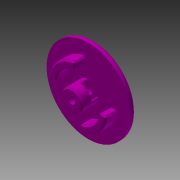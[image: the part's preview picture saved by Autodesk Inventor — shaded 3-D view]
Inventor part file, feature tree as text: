
AUTODESK INVENTOR PART (.ipt)
format: ipt  version: 2014 (Build 180170000, 170)  size: 237,056 bytes
history: native  units: in
note: dims shown in document units (in); Inventor stores cm internally (conversion verified against a paired STEP export)
features: extrude x8, sketch x8, fillet x4, pattern_circular x1, plane x1, chamfer x1
ambient origin geometry x8: Origin, YZ Plane, XZ Plane, XY Plane, X Axis, Y Axis, Z Axis, Center Point
bodies: Solid1 (feature_tree)
feature tree (23):
  extrude  "Extrusion1"  Depth=0.1in TaperAngle=0.0deg
  extrude  "Extrusion2"  Depth=0.3in TaperAngle=0.0deg
  extrude  "Extrusion3"  Depth=0.335in TaperAngle=0.0deg
  extrude  "Extrusion4"  Depth=0.0478in
  pattern_circular  "Circular Pattern1"  Count=2 Angle=360.0deg
  extrude  "Extrusion5"  Depth=0.02in
  extrude  "Extrusion6"  Depth=0.26in TaperAngle=0.0deg
  plane  "Work Plane1"
  extrude  "Extrusion7"  Depth=0.02in
  fillet  "Fillet1"  Radius=1.0in
  fillet  "Fillet2"  Radius=0.145in
  fillet  "Fillet3"  Radius=0.13in
  extrude  "Extrusion8"  Depth=0.02in TaperAngle=0.0deg
  chamfer  "Chamfer1"  Distance=0.05in
  fillet  "Fillet4"  Radius=0.05in
  sketch  "Sketch1"  dims[d0=1.5in d1=0.1in d2=0.0in]
  sketch  "Sketch2"  dims[d3=0.373in d4=0.3in d5=0.0in]
  sketch  "Sketch3"  dims[d6=0.1195in d7=0.335in d8=0.0in]
  sketch  "Sketch4"  dims[d9=0.0478in d10=0.0478in]
  sketch  "Sketch5"  dims[d11=0.3925in]
  sketch  "Sketch6"  dims[d12=0.5225in]
  sketch  "Sketch7"  dims[d13=0.2in d14=0.0in d15=0.7874in d16=360.0deg]
  sketch  "Sketch8"  dims[d18=0.152in d19=0.182in d20=0.26in d21=0.0in d22=0.125in d23=1.0in d24=0.0in d25=0.145in d26=0.13in d27=0.25in d28=0.0in d29=0.05in d30=0.05in d31=0.05in d32=0.233in d33=0.138in d34=0.0in d35=0.025in d36=0.125in d37=45.0deg d43=0.02in]
